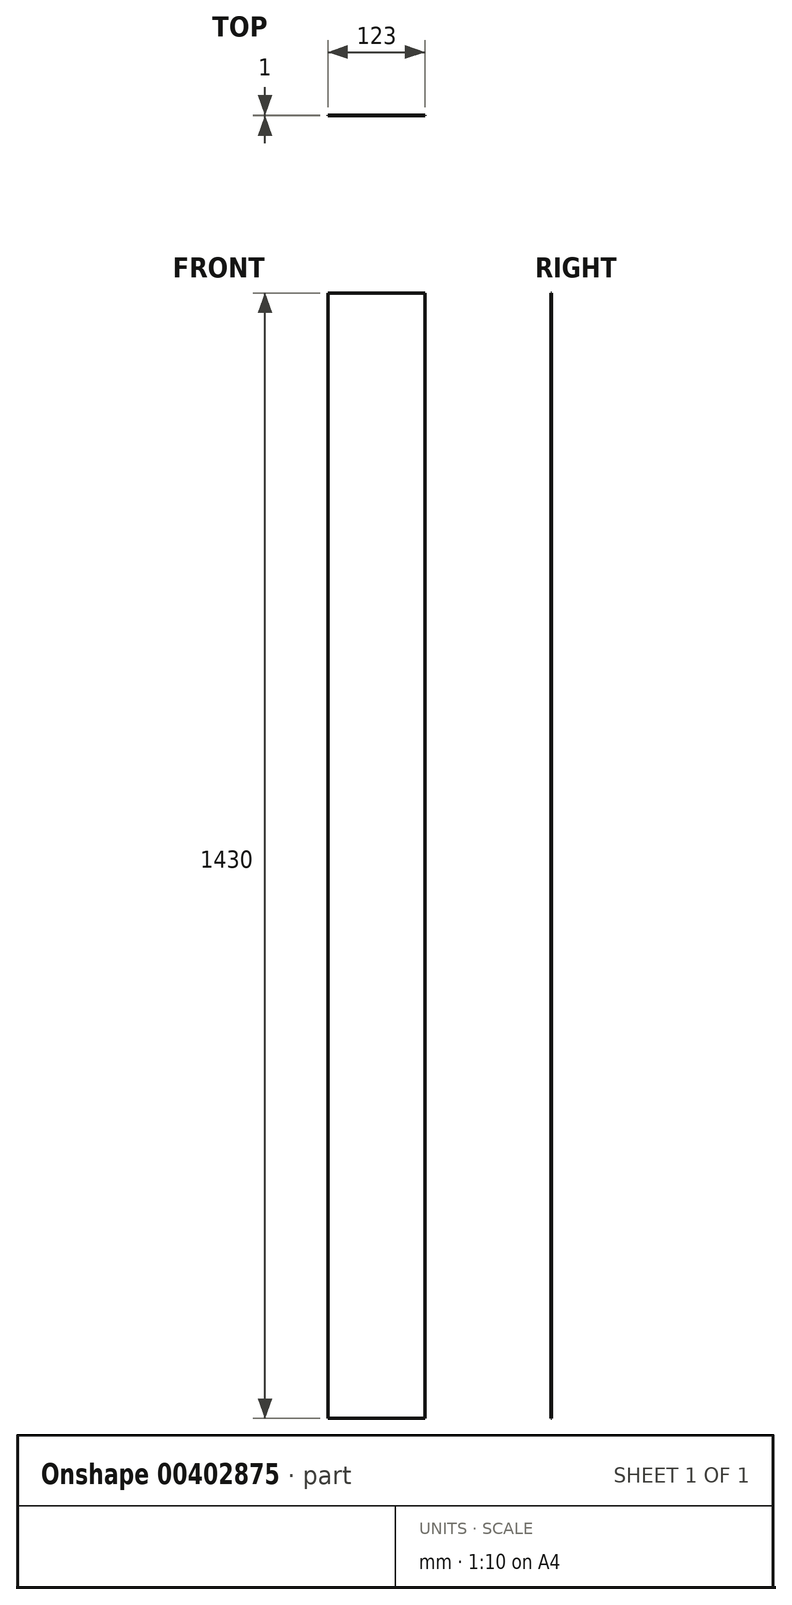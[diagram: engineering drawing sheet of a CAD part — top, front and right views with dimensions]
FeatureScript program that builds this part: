
annotation { "Feature Type Name" : "Feature", "Feature Type Description" : "" }
export const myFeature = defineFeature(function(context is Context, id is Id, definition is map)
    precondition{}
    {
        {
            var Q0;
            Q0=qCreatedBy(makeId("Front.planeOp"),FACE);
            var sketch = newSketch(context, id + "F0", { "sketchPlane" : qUnion([Q0])});
            skLineSegment(sketch, "E0.bottom", {"start": v(-61.5, 715) * mm, "end": v(61.5, 715) * mm});
            skLineSegment(sketch, "E0.top", {"start": v(-61.5, -715) * mm, "end": v(61.5, -715) * mm});
            skLineSegment(sketch, "E0.left", {"start": v(-61.5, 715) * mm, "end": v(-61.5, -715) * mm});
            skLineSegment(sketch, "E0.right", {"start": v(61.5, 715) * mm, "end": v(61.5, -715) * mm});
            skPoint(sketch, "E0.middle", {"position": v(0, 0) * mm});
            skSolve(sketch);
        }
        {
            var Q0;
            Q0=makeQuery(id+"F0.imprint","IMPRINT",FACE,{"disambiguationData":[TD([[makeQuery(id+"F0.imprint","IMPRINT",EDGE,{"derivedFrom":sQuery(id+"F0.wireOp",EDGE,"E0.bottom")}),-1.0]])]});
            extrude(context, id + "F1", {"entities" : qUnion([Q0]), "depth" : 1 * mm});
        }
    });
